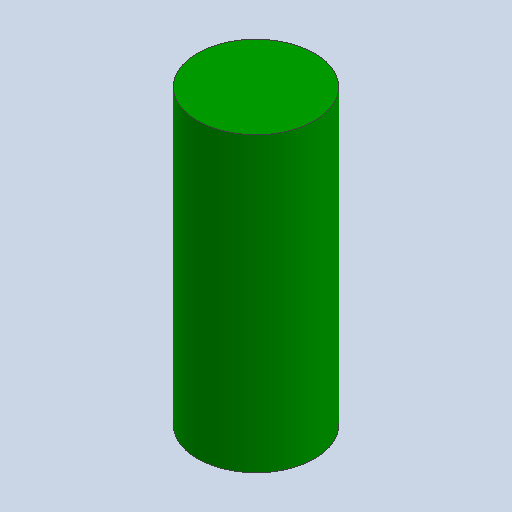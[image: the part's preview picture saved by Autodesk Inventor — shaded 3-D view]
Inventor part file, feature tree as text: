
AUTODESK INVENTOR PART (.ipt)
format: ipt  version: 2025.2 (Build 292293000, 293)  size: 89,600 bytes
history: native  units: in
note: dims shown in document units (in); Inventor stores cm internally (conversion verified against a paired STEP export)
features: other x3, sketch x1
ambient origin geometry x8: Origin, YZ Plane, XZ Plane, XY Plane, X Axis, Y Axis, Z Axis, Center Point
bodies: Solid1 (feature_tree)
feature tree (4):
  other  "26650(Green)_MIR3_MIR.ipt"
  other  "Solid1::26650(Green)_MIR3_MIR.ipt"
  other  "TaggingFeature1"
  sketch  "Sketch1"  dims[d0=0.3937in]
